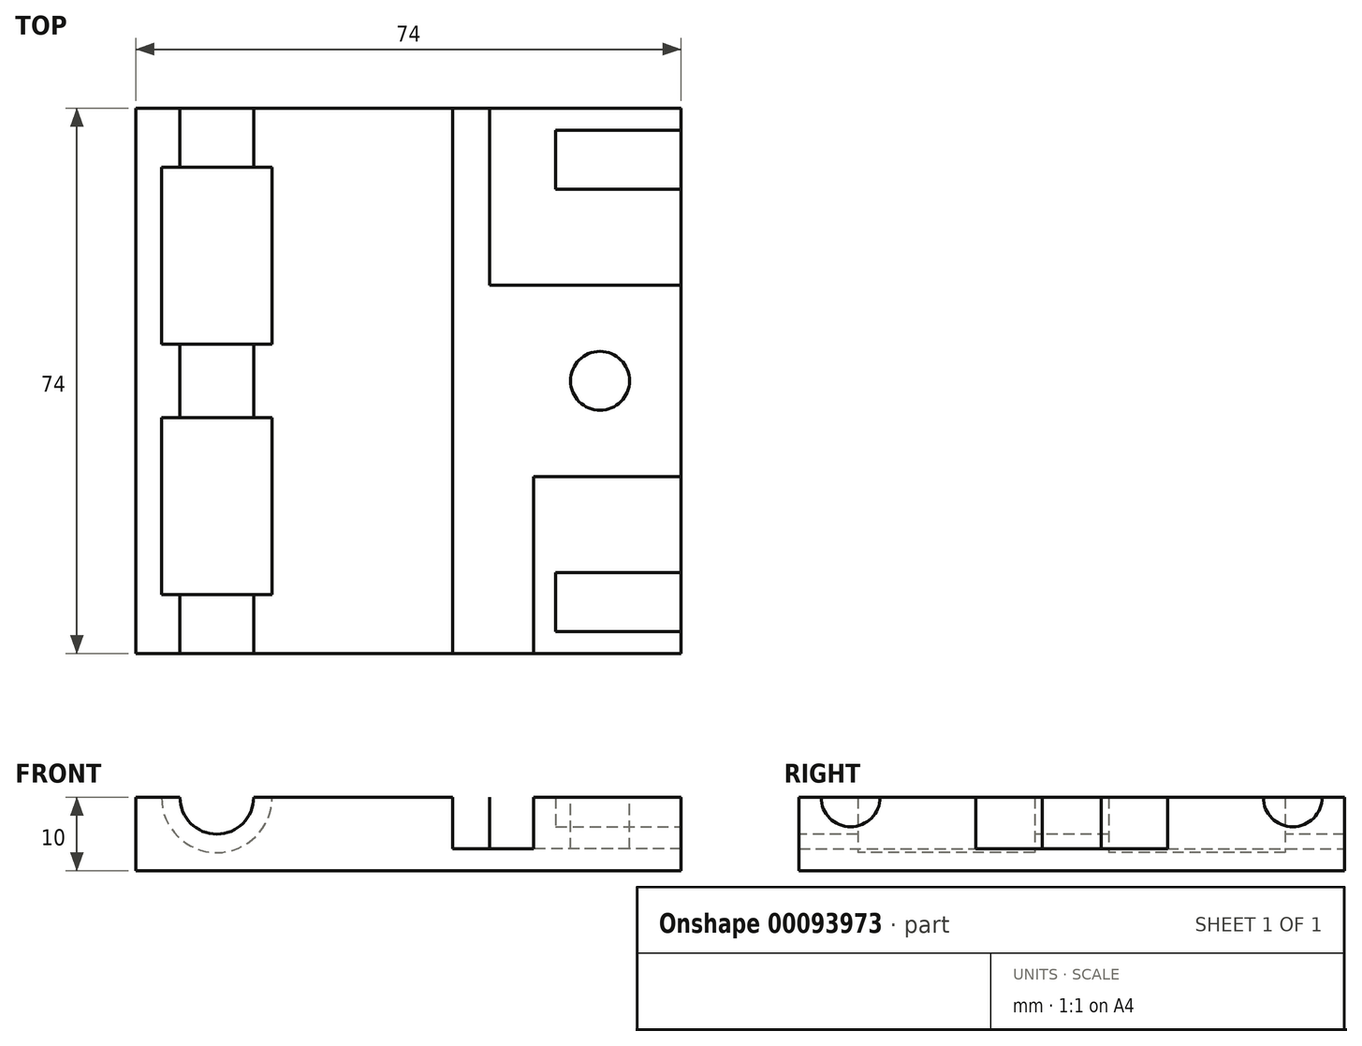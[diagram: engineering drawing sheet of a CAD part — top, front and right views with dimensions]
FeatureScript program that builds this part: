
annotation { "Feature Type Name" : "Feature", "Feature Type Description" : "" }
export const myFeature = defineFeature(function(context is Context, id is Id, definition is map)
    precondition{}
    {
        {
            var Q0;
            Q0=qCreatedBy(makeId("Top.planeOp"),FACE);
            var sketch = newSketch(context, id + "F0", { "sketchPlane" : qUnion([Q0])});
            skCircle(sketch, "E0", {"center": v(0, 0) * mm, "radius": 11 * mm, "construction": true});
            skCircle(sketch, "E1", {"center": v(0, 0) * mm, "radius": 4 * mm});
            skLineSegment(sketch, "E2", {"start": v(-9, -13) * mm, "end": v(11, -13) * mm});
            skLineSegment(sketch, "E3", {"start": v(11, -37) * mm, "end": v(-9, -37) * mm});
            skLineSegment(sketch, "E4", {"start": v(-9, -37) * mm, "end": v(-9, -13) * mm});
            skLineSegment(sketch, "E5", {"start": v(11, 13) * mm, "end": v(-15, 13) * mm});
            skLineSegment(sketch, "E6", {"start": v(-20, 13) * mm, "end": v(-20, -37) * mm});
            skLineSegment(sketch, "E7", {"start": v(-20, -37) * mm, "end": v(-63, -37) * mm});
            skLineSegment(sketch, "E8", {"start": v(-63, -37) * mm, "end": v(-63, 37) * mm});
            skLineSegment(sketch, "E9", {"start": v(-63, 37) * mm, "end": v(-20, 37) * mm});
            skLineSegment(sketch, "E10", {"start": v(11, 37) * mm, "end": v(11, 34) * mm});
            skLineSegment(sketch, "E11", {"start": v(11, 34) * mm, "end": v(-6, 34) * mm});
            skLineSegment(sketch, "E12", {"start": v(-6, 34) * mm, "end": v(-6, 30) * mm});
            skLineSegment(sketch, "E13", {"start": v(-52, 37) * mm, "end": v(-52, -37) * mm});
            skLineSegment(sketch, "E14", {"start": v(-47, 0) * mm, "end": v(-47, 5) * mm});
            skLineSegment(sketch, "E15", {"start": v(-47, 5) * mm, "end": v(-44.5, 5) * mm});
            skLineSegment(sketch, "E16", {"start": v(-44.5, 5) * mm, "end": v(-44.5, 29) * mm});
            skLineSegment(sketch, "E17", {"start": v(-44.5, 29) * mm, "end": v(-47, 29) * mm});
            skLineSegment(sketch, "E18", {"start": v(-47, 29) * mm, "end": v(-47, 37) * mm});
            skLineSegment(sketch, "E19.MirrorCS", {"start": v(-47, 0) * mm, "end": v(-47, -5) * mm});
            skLineSegment(sketch, "E20.MirrorCS", {"start": v(-47, -5) * mm, "end": v(-44.5, -5) * mm});
            skLineSegment(sketch, "E21.MirrorCS", {"start": v(-44.5, -5) * mm, "end": v(-44.5, -29) * mm});
            skLineSegment(sketch, "E22.MirrorCS", {"start": v(-44.5, -29) * mm, "end": v(-47, -29) * mm});
            skLineSegment(sketch, "E23.MirrorCS", {"start": v(-47, -29) * mm, "end": v(-47, -37) * mm});
            skLineSegment(sketch, "E24", {"start": v(-20, -37) * mm, "end": v(-9, -37) * mm});
            skLineSegment(sketch, "E25", {"start": v(11, -37) * mm, "end": v(11, -13) * mm});
            skLineSegment(sketch, "E26", {"start": v(11, 13) * mm, "end": v(11, 34) * mm});
            skLineSegment(sketch, "E27", {"start": v(11, -13) * mm, "end": v(11, 13) * mm});
            skLineSegment(sketch, "E28", {"start": v(-6, 30) * mm, "end": v(11, 30) * mm});
            skLineSegment(sketch, "E29.MirrorCS", {"start": v(-6, -30) * mm, "end": v(11, -30) * mm});
            skLineSegment(sketch, "E30.MirrorCS", {"start": v(-6, -34) * mm, "end": v(-6, -30) * mm});
            skLineSegment(sketch, "E31.MirrorCS", {"start": v(11, -34) * mm, "end": v(-6, -34) * mm});
            skLineSegment(sketch, "E32", {"start": v(-20, 13) * mm, "end": v(-20, 37) * mm});
            skLineSegment(sketch, "E33", {"start": v(-15, 13) * mm, "end": v(-15, 37) * mm});
            skLineSegment(sketch, "E34.trimOffspring", {"start": v(-15, 37) * mm, "end": v(11, 37) * mm});
            skLineSegment(sketch, "E35", {"start": v(-20, 37) * mm, "end": v(-15, 37) * mm});
            skSolve(sketch);
        }
        {
            var Q0;
            {var subQ0=sQuery(id+"F0.wireOp",EDGE,"E8");Q0=makeQuery(id+"F0.imprint","IMPRINT",FACE,{"disambiguationData":[TD([[makeQuery(id+"F0.imprint","IMPRINT",EDGE,{"derivedFrom":subQ0}),-1.0]])]});}
            var Q1;
            {var subQ0=sQuery(id+"F0.wireOp",EDGE,"E11");Q1=makeQuery(id+"F0.imprint","IMPRINT",FACE,{"disambiguationData":[TD([[makeQuery(id+"F0.imprint","IMPRINT",EDGE,{"derivedFrom":subQ0}),1.0]])]});}
            var Q2;
            {var subQ0=sQuery(id+"F0.wireOp",EDGE,"E29.MirrorCS");Q2=makeQuery(id+"F0.imprint","IMPRINT",FACE,{"disambiguationData":[TD([[makeQuery(id+"F0.imprint","IMPRINT",EDGE,{"derivedFrom":subQ0}),-1.0]])]});}
            var Q3;
            {var subQ3=sQuery(id+"F0.wireOp",EDGE,"E2");Q3=makeQuery(id+"F0.imprint","IMPRINT",FACE,{"disambiguationData":[TD([[makeQuery(id+"F0.imprint","IMPRINT",EDGE,{"derivedFrom":subQ3}),-1.0]])]});}
            var Q4;
            {var subQ1=sQuery(id+"F0.wireOp",EDGE,"E13");Q4=makeQuery(id+"F0.imprint","IMPRINT",FACE,{"disambiguationData":[TD([[makeQuery(id+"F0.imprint","IMPRINT",EDGE,{"derivedFrom":subQ1}),1.0]])]});}
            var Q5;
            {var subQ0=sQuery(id+"F0.wireOp",EDGE,"E5");Q5=makeQuery(id+"F0.imprint","IMPRINT",FACE,{"disambiguationData":[TD([[makeQuery(id+"F0.imprint","IMPRINT",EDGE,{"derivedFrom":subQ0}),-1.0]])]});}
            var Q6;
            Q6=makeQuery(id+"F0.imprint","IMPRINT",FACE,{"disambiguationData":[TD([[makeQuery(id+"F0.imprint","IMPRINT",EDGE,{"derivedFrom":sQuery(id+"F0.wireOp",EDGE,"E1")}),1.0]])]});
            var Q7;
            Q7=makeQuery(id+"F0.imprint","IMPRINT",FACE,{"disambiguationData":[TD([[makeQuery(id+"F0.imprint","IMPRINT",EDGE,{"derivedFrom":sQuery(id+"F0.wireOp",EDGE,"E1")}),-1.0]])]});
            var Q8;
            {var subQ3=sQuery(id+"F0.wireOp",EDGE,"E6");Q8=makeQuery(id+"F0.imprint","IMPRINT",FACE,{"disambiguationData":[TD([[makeQuery(id+"F0.imprint","IMPRINT",EDGE,{"derivedFrom":subQ3}),-1.0]])]});}
            extrude(context, id + "F1", {"entities" : qUnion([Q0, Q1, Q2, Q3, Q4, Q5, Q6, Q7, Q8]), "oppositeDirection" : true, "depth" : 10 * mm});
        }
        {
            var Q0;
            {var subQ1=sQuery(id+"F0.wireOp",EDGE,"E13");Q0=makeQuery(id+"F0.imprint","IMPRINT",FACE,{"disambiguationData":[TD([[makeQuery(id+"F0.imprint","IMPRINT",EDGE,{"derivedFrom":subQ1}),1.0]])]});}
            var Q1;
            Q1=sQuery(id+"F0.wireOp",EDGE,"E13");
            revolve(context, id + "F2", {"operationType" : NewBodyOperationType.REMOVE, "entities" : qUnion([Q0]), "axis" : qUnion([Q1]), "revolveType" : RevolveType.FULL, "oppositeDirection" : true});
        }
        {
            var Q0;
            {var subQ0=sQuery(id+"F0.wireOp",EDGE,"E11");Q0=makeQuery(id+"F0.imprint","IMPRINT",FACE,{"disambiguationData":[TD([[makeQuery(id+"F0.imprint","IMPRINT",EDGE,{"derivedFrom":subQ0}),1.0]])]});}
            var Q1;
            Q1=sQuery(id+"F0.wireOp",EDGE,"E28");
            revolve(context, id + "F3", {"operationType" : NewBodyOperationType.REMOVE, "entities" : qUnion([Q0]), "axis" : qUnion([Q1]), "revolveType" : RevolveType.FULL, "oppositeDirection" : true});
        }
        {
            var Q0;
            {var subQ0=sQuery(id+"F0.wireOp",EDGE,"E29.MirrorCS");Q0=makeQuery(id+"F0.imprint","IMPRINT",FACE,{"disambiguationData":[TD([[makeQuery(id+"F0.imprint","IMPRINT",EDGE,{"derivedFrom":subQ0}),-1.0]])]});}
            var Q1;
            Q1=sQuery(id+"F0.wireOp",EDGE,"E29.MirrorCS");
            revolve(context, id + "F4", {"operationType" : NewBodyOperationType.REMOVE, "entities" : qUnion([Q0]), "axis" : qUnion([Q1]), "revolveType" : RevolveType.FULL, "oppositeDirection" : true});
        }
        {
            var Q0;
            Q0=makeQuery(id+"F0.imprint","IMPRINT",FACE,{"disambiguationData":[TD([[makeQuery(id+"F0.imprint","IMPRINT",EDGE,{"derivedFrom":sQuery(id+"F0.wireOp",EDGE,"E1")}),-1.0]])]});
            extrude(context, id + "F5", {"entities" : qUnion([Q0]), "operationType" : NewBodyOperationType.REMOVE, "oppositeDirection" : true, "depth" : 7 * mm});
        }
    });
